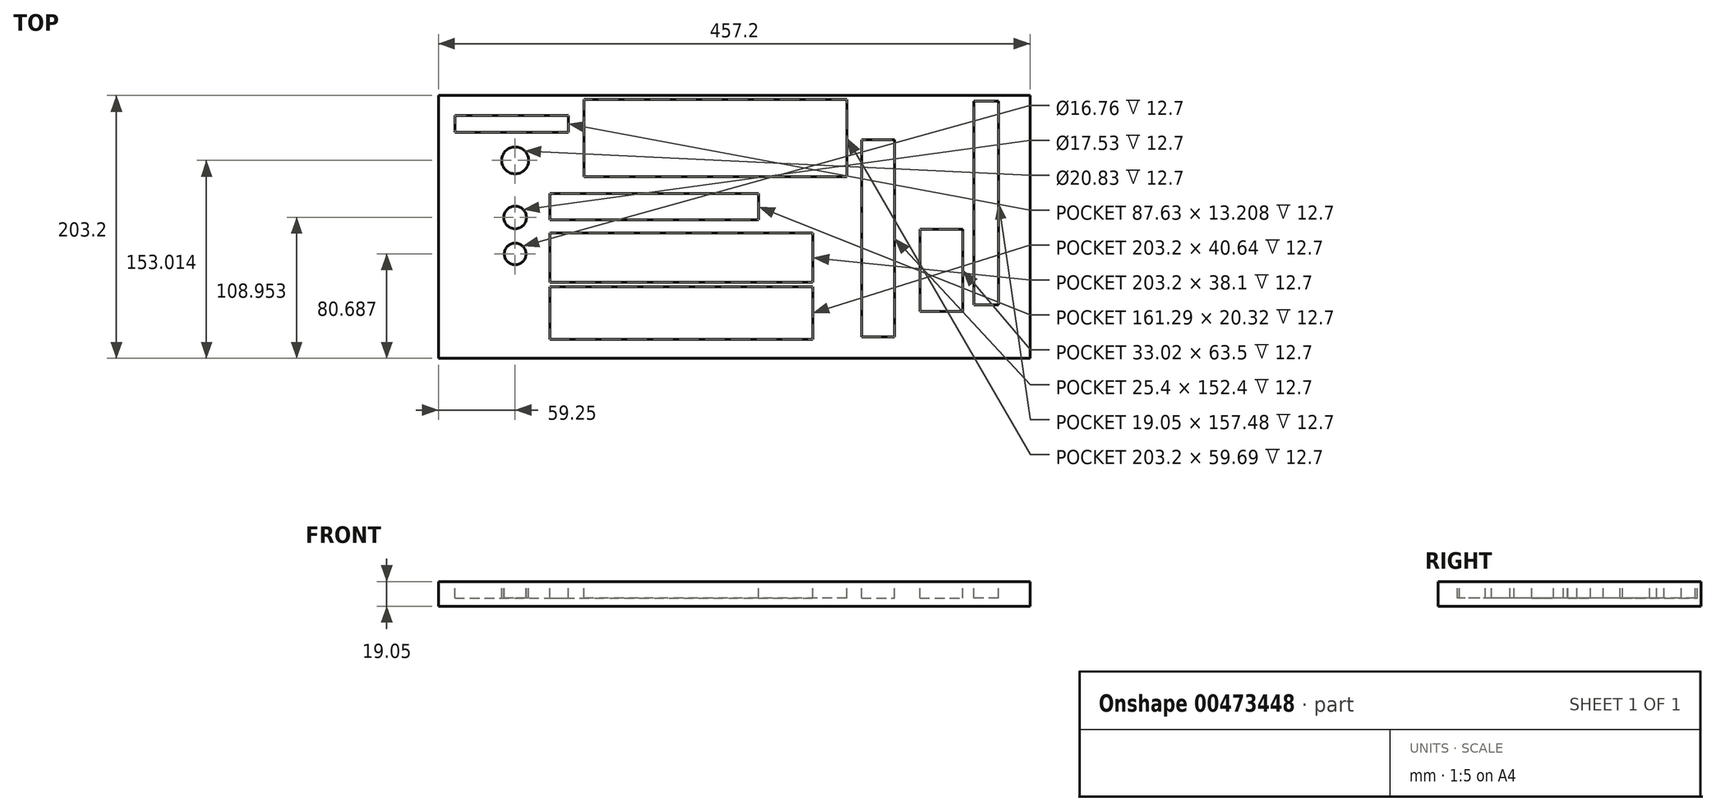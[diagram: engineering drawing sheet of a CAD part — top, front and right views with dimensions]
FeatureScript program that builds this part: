
annotation { "Feature Type Name" : "Feature", "Feature Type Description" : "" }
export const myFeature = defineFeature(function(context is Context, id is Id, definition is map)
    precondition{}
    {
        {
            var Q0;
            Q0=qCreatedBy(makeId("Top.planeOp"),FACE);
            var sketch = newSketch(context, id + "F0", { "sketchPlane" : qUnion([Q0])});
            skLineSegment(sketch, "E0.bottom", {"start": v(-396.86, 144.47) * mm, "end": v(60.34, 144.47) * mm});
            skLineSegment(sketch, "E0.top", {"start": v(-396.86, -58.73) * mm, "end": v(60.34, -58.73) * mm});
            skLineSegment(sketch, "E0.left", {"start": v(-396.86, 144.47) * mm, "end": v(-396.86, -58.73) * mm});
            skLineSegment(sketch, "E0.right", {"start": v(60.34, 144.47) * mm, "end": v(60.34, -58.73) * mm});
            skSolve(sketch);
        }
        {
            var Q0;
            Q0 = qSketchRegion(id + "F0", true);
            extrude(context, id + "F1", {"entities" : qUnion([Q0]), "depth" : 19.05 * mm});
        }
        {
            var Q0;
            Q0=makeQuery(id+"F1.opExtrude","CAP_FACE",FACE,{"disambiguationData":[OSD([sQuery(id+"F0.wireOp",EDGE,"E0.bottom"),sQuery(id+"F0.wireOp",EDGE,"E0.top"),sQuery(id+"F0.wireOp",EDGE,"E0.left"),sQuery(id+"F0.wireOp",EDGE,"E0.right")])],"isStart":false});
            var sketch = newSketch(context, id + "F2", { "sketchPlane" : qUnion([Q0])});
            skLineSegment(sketch, "E1.bottom", {"start": v(-81.2, 81.81) * mm, "end": v(-284.4, 81.81) * mm});
            skLineSegment(sketch, "E1.top", {"start": v(-81.2, 141.5) * mm, "end": v(-284.4, 141.5) * mm});
            skLineSegment(sketch, "E1.left", {"start": v(-81.2, 81.81) * mm, "end": v(-81.2, 141.5) * mm});
            skLineSegment(sketch, "E1.right", {"start": v(-284.4, 81.81) * mm, "end": v(-284.4, 141.5) * mm});
            skSolve(sketch);
        }
        {
            var Q0;
            Q0=makeQuery(id+"F2.imprint","IMPRINT",FACE,{"disambiguationData":[TD([[makeQuery(id+"F2.imprint","IMPRINT",EDGE,{"derivedFrom":sQuery(id+"F2.wireOp",EDGE,"E1.bottom")}),1.0]])]});
            var sketch = newSketch(context, id + "F3", { "sketchPlane" : qUnion([Q0])});
            skCircle(sketch, "E2", {"center": v(-337.6, 94.28) * mm, "radius": 10.41 * mm});
            skCircle(sketch, "E3", {"center": v(-337.6, 50.22) * mm, "radius": 8.76 * mm});
            skCircle(sketch, "E4", {"center": v(-337.6, 21.96) * mm, "radius": 8.38 * mm});
            skSolve(sketch);
        }
        {
            var Q0;
            Q0=sQuery(id+"F3.wireOp",EDGE,"E2");
            var Q1;
            Q1=sQuery(id+"F3.wireOp",EDGE,"E3");
            var Q2;
            Q2=sQuery(id+"F3.wireOp",EDGE,"E4");
            var Q3;
            Q3 = qConstructionFilter(qBodyType(qCreatedBy(id + "F2" ,EDGE), BodyType.WIRE), ConstructionObject.NO);
            extrude(context, id + "F4", {"bodyType" : ToolBodyType.SURFACE, "surfaceEntities" : qUnion([Q0, Q1, Q2, Q3]), "depth" : -12.7 * mm});
        }
        {
            var Q0;
            Q0 = qSketchRegion(id + "F2", true);
            var Q1;
            Q1 = qSketchRegion(id + "F3", true);
            extrude(context, id + "F5", {"entities" : qUnion([Q0, Q1]), "operationType" : NewBodyOperationType.ADD, "depth" : -19.05 * mm});
        }
        {
            var Q0;
            Q0=makeQuery(id+"F1.opExtrude","CAP_FACE",FACE,{"disambiguationData":[OSD([sQuery(id+"F0.wireOp",EDGE,"E0.bottom"),sQuery(id+"F0.wireOp",EDGE,"E0.top"),sQuery(id+"F0.wireOp",EDGE,"E0.left"),sQuery(id+"F0.wireOp",EDGE,"E0.right")])],"isStart":false});
            var sketch = newSketch(context, id + "F6", { "sketchPlane" : qUnion([Q0])});
            skLineSegment(sketch, "E5.bottom", {"start": v(-384.16, 115.9) * mm, "end": v(-296.53, 115.9) * mm});
            skLineSegment(sketch, "E5.top", {"start": v(-384.16, 129.1) * mm, "end": v(-296.53, 129.1) * mm});
            skLineSegment(sketch, "E5.left", {"start": v(-384.16, 115.9) * mm, "end": v(-384.16, 129.1) * mm});
            skLineSegment(sketch, "E5.right", {"start": v(-296.53, 115.9) * mm, "end": v(-296.53, 129.1) * mm});
            skSolve(sketch);
        }
        {
            var Q0;
            Q0=makeQuery(id+"F6.imprint","IMPRINT",FACE,{"disambiguationData":[TD([[makeQuery(id+"F6.imprint","IMPRINT",EDGE,{"derivedFrom":sQuery(id+"F6.wireOp",EDGE,"E5.bottom")}),-1.0]])]});
            var sketch = newSketch(context, id + "F7", { "sketchPlane" : qUnion([Q0])});
            skLineSegment(sketch, "E6.bottom", {"start": v(35.9, 140.01) * mm, "end": v(16.85, 140.01) * mm});
            skLineSegment(sketch, "E6.top", {"start": v(35.9, -17.47) * mm, "end": v(16.85, -17.47) * mm});
            skLineSegment(sketch, "E6.left", {"start": v(35.9, 140.01) * mm, "end": v(35.9, -17.47) * mm});
            skLineSegment(sketch, "E6.right", {"start": v(16.85, 140.01) * mm, "end": v(16.85, -17.47) * mm});
            skSolve(sketch);
        }
        {
            var Q0;
            Q0=makeQuery(id+"F6.imprint","IMPRINT",FACE,{"disambiguationData":[TD([[makeQuery(id+"F6.imprint","IMPRINT",EDGE,{"derivedFrom":sQuery(id+"F6.wireOp",EDGE,"E5.bottom")}),-1.0]])]});
            var sketch = newSketch(context, id + "F8", { "sketchPlane" : qUnion([Q0])});
            skLineSegment(sketch, "E7.bottom", {"start": v(-310.77, 68.72) * mm, "end": v(-149.48, 68.72) * mm});
            skLineSegment(sketch, "E7.top", {"start": v(-310.77, 48.4) * mm, "end": v(-149.48, 48.4) * mm});
            skLineSegment(sketch, "E7.left", {"start": v(-310.77, 68.72) * mm, "end": v(-310.77, 48.4) * mm});
            skLineSegment(sketch, "E7.right", {"start": v(-149.48, 68.72) * mm, "end": v(-149.48, 48.4) * mm});
            skLineSegment(sketch, "E8.bottom", {"start": v(-310.77, 38.1) * mm, "end": v(-107.57, 38.1) * mm});
            skLineSegment(sketch, "E8.top", {"start": v(-310.77, 0) * mm, "end": v(-107.57, 0) * mm});
            skLineSegment(sketch, "E8.left", {"start": v(-310.77, 38.1) * mm, "end": v(-310.77, 0) * mm});
            skLineSegment(sketch, "E8.right", {"start": v(-107.57, 38.1) * mm, "end": v(-107.57, 0) * mm});
            skLineSegment(sketch, "E9.bottom", {"start": v(-310.77, -3.28) * mm, "end": v(-107.57, -3.28) * mm});
            skLineSegment(sketch, "E9.top", {"start": v(-310.77, -43.92) * mm, "end": v(-107.57, -43.92) * mm});
            skLineSegment(sketch, "E9.left", {"start": v(-310.77, -3.28) * mm, "end": v(-310.77, -43.92) * mm});
            skLineSegment(sketch, "E9.right", {"start": v(-107.57, -3.28) * mm, "end": v(-107.57, -43.92) * mm});
            skSolve(sketch);
        }
        {
            var Q0;
            Q0=makeQuery(id+"F7.imprint","IMPRINT",FACE,{"disambiguationData":[TD([[makeQuery(id+"F7.imprint","IMPRINT",EDGE,{"derivedFrom":sQuery(id+"F7.wireOp",EDGE,"E6.bottom")}),-1.0]])]});
            var sketch = newSketch(context, id + "F9", { "sketchPlane" : qUnion([Q0])});
            skLineSegment(sketch, "E10.bottom", {"start": v(-69.88, 110.21) * mm, "end": v(-44.48, 110.21) * mm});
            skLineSegment(sketch, "E10.top", {"start": v(-69.88, -42.19) * mm, "end": v(-44.48, -42.19) * mm});
            skLineSegment(sketch, "E10.left", {"start": v(-69.88, 110.21) * mm, "end": v(-69.88, -42.19) * mm});
            skLineSegment(sketch, "E10.right", {"start": v(-44.48, 110.21) * mm, "end": v(-44.48, -42.19) * mm});
            skSolve(sketch);
        }
        {
            var Q0;
            Q0=makeQuery(id+"F6.imprint","IMPRINT",FACE,{"disambiguationData":[TD([[makeQuery(id+"F6.imprint","IMPRINT",EDGE,{"derivedFrom":sQuery(id+"F6.wireOp",EDGE,"E5.bottom")}),-1.0]])]});
            var sketch = newSketch(context, id + "F10", { "sketchPlane" : qUnion([Q0])});
            skLineSegment(sketch, "E11.bottom", {"start": v(-24.76, 41.07) * mm, "end": v(8.26, 41.07) * mm});
            skLineSegment(sketch, "E11.top", {"start": v(-24.76, -22.43) * mm, "end": v(8.26, -22.43) * mm});
            skLineSegment(sketch, "E11.left", {"start": v(-24.76, 41.07) * mm, "end": v(-24.76, -22.43) * mm});
            skLineSegment(sketch, "E11.right", {"start": v(8.26, 41.07) * mm, "end": v(8.26, -22.43) * mm});
            skSolve(sketch);
        }
        {
            var Q0;
            Q0=makeQuery(id+"F6.imprint","IMPRINT",FACE,{"disambiguationData":[TD([[makeQuery(id+"F6.imprint","IMPRINT",EDGE,{"derivedFrom":sQuery(id+"F6.wireOp",EDGE,"E5.bottom")}),1.0]])]});
            extrude(context, id + "F11", {"entities" : qUnion([Q0]), "operationType" : NewBodyOperationType.REMOVE, "oppositeDirection" : true, "depth" : 12.7 * mm});
        }
        {
            var Q0;
            Q0=makeQuery(id+"F8.imprint","IMPRINT",FACE,{"disambiguationData":[TD([[makeQuery(id+"F8.imprint","IMPRINT",EDGE,{"derivedFrom":sQuery(id+"F8.wireOp",EDGE,"E7.bottom")}),-1.0]])]});
            var Q1;
            Q1=makeQuery(id+"F8.imprint","IMPRINT",FACE,{"disambiguationData":[TD([[makeQuery(id+"F8.imprint","IMPRINT",EDGE,{"derivedFrom":sQuery(id+"F8.wireOp",EDGE,"E8.bottom")}),-1.0]])]});
            var Q2;
            Q2=makeQuery(id+"F8.imprint","IMPRINT",FACE,{"disambiguationData":[TD([[makeQuery(id+"F8.imprint","IMPRINT",EDGE,{"derivedFrom":sQuery(id+"F8.wireOp",EDGE,"E9.bottom")}),-1.0]])]});
            extrude(context, id + "F12", {"entities" : qUnion([Q0, Q1, Q2]), "operationType" : NewBodyOperationType.REMOVE, "oppositeDirection" : true, "depth" : 12.7 * mm});
        }
        {
            var Q0;
            Q0=makeQuery(id+"F9.imprint","IMPRINT",FACE,{"disambiguationData":[TD([[makeQuery(id+"F9.imprint","IMPRINT",EDGE,{"derivedFrom":sQuery(id+"F9.wireOp",EDGE,"E10.bottom")}),-1.0]])]});
            var Q1;
            Q1=makeQuery(id+"F10.imprint","IMPRINT",FACE,{"disambiguationData":[TD([[makeQuery(id+"F10.imprint","IMPRINT",EDGE,{"derivedFrom":sQuery(id+"F10.wireOp",EDGE,"E11.bottom")}),-1.0]])]});
            extrude(context, id + "F13", {"entities" : qUnion([Q0, Q1]), "operationType" : NewBodyOperationType.REMOVE, "oppositeDirection" : true, "depth" : 12.7 * mm});
        }
        {
            var Q0;
            Q0=makeQuery(id+"F7.imprint","IMPRINT",FACE,{"disambiguationData":[TD([[makeQuery(id+"F7.imprint","IMPRINT",EDGE,{"derivedFrom":sQuery(id+"F7.wireOp",EDGE,"E6.bottom")}),1.0]])]});
            extrude(context, id + "F14", {"entities" : qUnion([Q0]), "operationType" : NewBodyOperationType.REMOVE, "oppositeDirection" : true, "depth" : 12.7 * mm});
        }
        {
            var Q0;
            Q0 = qSketchRegion(id + "F2", true);
            extrude(context, id + "F15", {"entities" : qUnion([Q0]), "operationType" : NewBodyOperationType.REMOVE, "oppositeDirection" : true, "depth" : 12.7 * mm});
        }
        {
            var Q0;
            Q0 = qSketchRegion(id + "F3", true);
            extrude(context, id + "F16", {"entities" : qUnion([Q0]), "operationType" : NewBodyOperationType.REMOVE, "oppositeDirection" : true, "depth" : 12.7 * mm});
        }
    });
